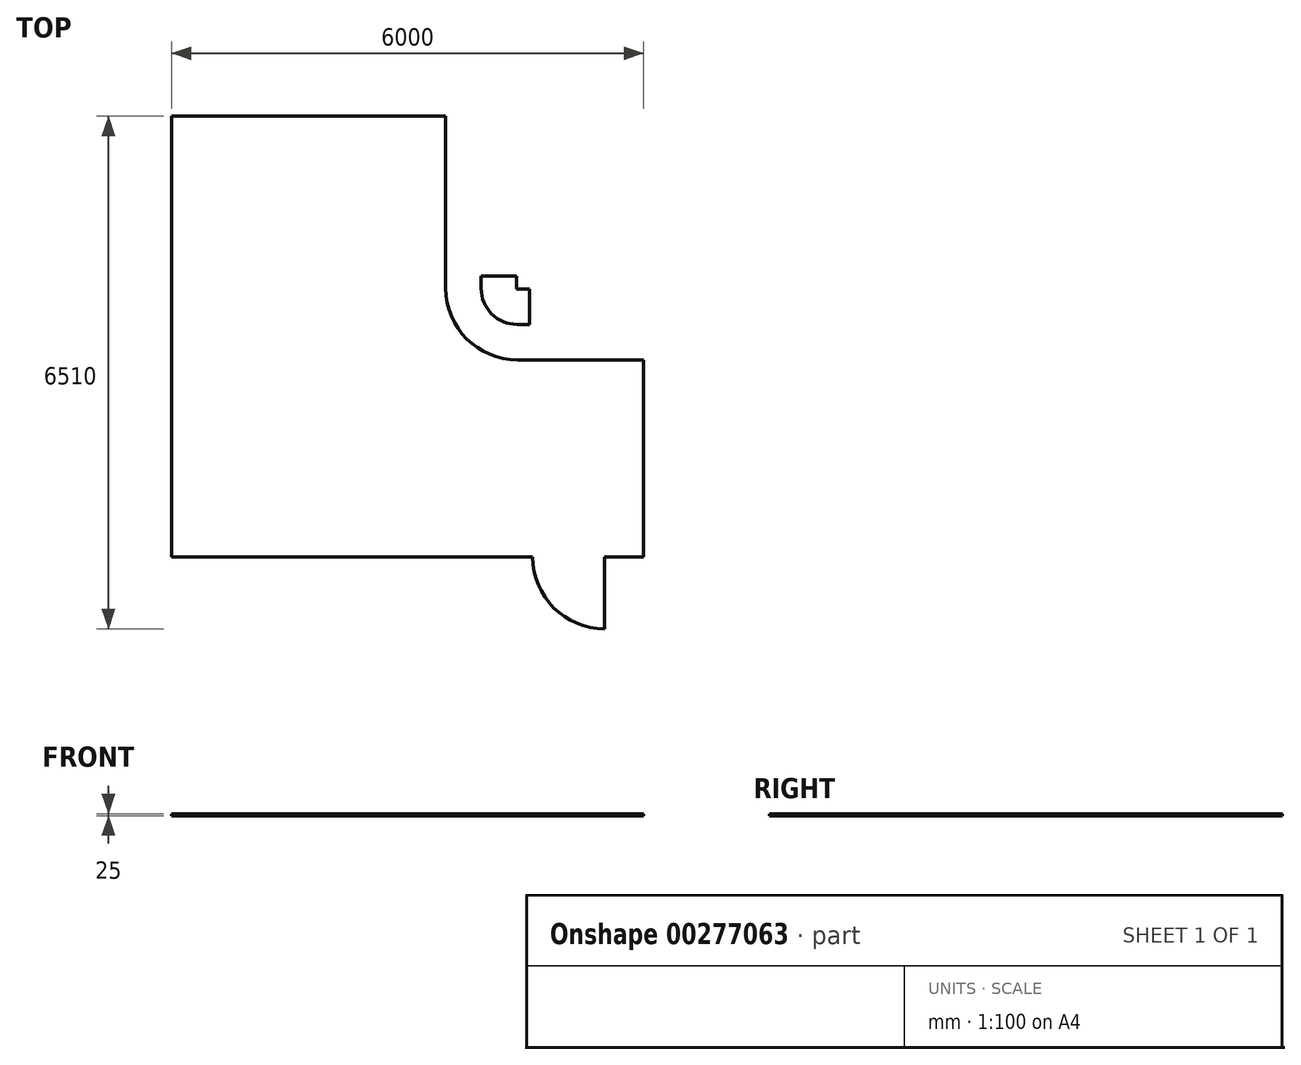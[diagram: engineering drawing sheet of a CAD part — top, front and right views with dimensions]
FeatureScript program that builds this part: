
annotation { "Feature Type Name" : "Feature", "Feature Type Description" : "" }
export const myFeature = defineFeature(function(context is Context, id is Id, definition is map)
    precondition{}
    {
        {
            var Q0;
            Q0=qCreatedBy(makeId("Top.planeOp"),FACE);
            var sketch = newSketch(context, id + "F0", { "sketchPlane" : qUnion([Q0])});
            skLineSegment(sketch, "E0", {"start": v(0, 0) * mm, "end": v(4590, 0) * mm});
            skLineSegment(sketch, "E1", {"start": v(6000, 0) * mm, "end": v(6000, 2505) * mm});
            skLineSegment(sketch, "E2", {"start": v(0, 0) * mm, "end": v(0, 5600) * mm});
            skLineSegment(sketch, "E3", {"start": v(0, 5600) * mm, "end": v(3485, 5600) * mm});
            skLineSegment(sketch, "E4", {"start": v(6000, 2505) * mm, "end": v(6000, 3405) * mm});
            skLineSegment(sketch, "E5", {"start": v(6000, 2505) * mm, "end": v(4395, 2505) * mm});
            skLineSegment(sketch, "E6", {"start": v(3485, 5600) * mm, "end": v(3485, 5527.98) * mm});
            skPoint(sketch, "E7.end.orphan", {"position": v(3485, 5527.98) * mm});
            skLineSegment(sketch, "E8", {"start": v(3485, 3415) * mm, "end": v(3485, 5600) * mm});
            skLineSegment(sketch, "E9", {"start": v(3485, 5600) * mm, "end": v(4385, 5600) * mm});
            skLineSegment(sketch, "E10", {"start": v(4385, 5600) * mm, "end": v(4385, 3405) * mm});
            skLineSegment(sketch, "E11", {"start": v(6000, 3405) * mm, "end": v(4385, 3405) * mm});
            skLineSegment(sketch, "E12", {"start": v(6000, 3405) * mm, "end": v(6000, 2955) * mm});
            skLineSegment(sketch, "E13", {"start": v(6000, 2955) * mm, "end": v(4385, 2955) * mm});
            skLineSegment(sketch, "E14", {"start": v(3935, 5600) * mm, "end": v(3935, 3410) * mm});
            skLineSegment(sketch, "E15", {"start": v(3485, 5600) * mm, "end": v(3485, 5310) * mm});
            skLineSegment(sketch, "E16", {"start": v(3485, 5310) * mm, "end": v(4385, 5310) * mm});
            skLineSegment(sketch, "E17", {"start": v(4385, 5310) * mm, "end": v(4385, 5020) * mm});
            skLineSegment(sketch, "E18", {"start": v(4385, 5020) * mm, "end": v(3485, 5020) * mm});
            skLineSegment(sketch, "E19", {"start": v(3485, 5020) * mm, "end": v(3485, 4730) * mm});
            skLineSegment(sketch, "E20", {"start": v(3485, 4730) * mm, "end": v(4385, 4730) * mm});
            skLineSegment(sketch, "E21", {"start": v(4385, 4730) * mm, "end": v(4385, 4440) * mm});
            skLineSegment(sketch, "E22", {"start": v(4385, 4440) * mm, "end": v(3485, 4440) * mm});
            skLineSegment(sketch, "E23", {"start": v(3485, 4440) * mm, "end": v(3485, 4150) * mm});
            skLineSegment(sketch, "E24", {"start": v(3485, 4150) * mm, "end": v(4385, 4150) * mm});
            skLineSegment(sketch, "E25", {"start": v(4385, 4150) * mm, "end": v(4385, 3860) * mm});
            skLineSegment(sketch, "E26", {"start": v(4385, 3860) * mm, "end": v(3485, 3860) * mm});
            skLineSegment(sketch, "E27", {"start": v(3485, 3860) * mm, "end": v(3485, 3570) * mm});
            skLineSegment(sketch, "E28", {"start": v(3485, 3570) * mm, "end": v(4385, 3570) * mm});
            skLineSegment(sketch, "E29", {"start": v(4390, 2955) * mm, "end": v(4385, 2955) * mm});
            skArc(sketch, "E30.filletArc", {"start": v(3935, 3410) * mm, "mid": v(4068.27, 3088.27) * mm, "end": v(4390, 2955) * mm});
            skPoint(sketch, "E31.visualSharp", {"position": v(3485, 2505) * mm});
            skArc(sketch, "E31.filletArc", {"start": v(3485, 3415) * mm, "mid": v(3751.53, 2771.53) * mm, "end": v(4395, 2505) * mm});
            skLineSegment(sketch, "E32", {"start": v(6000, 3405) * mm, "end": v(5710, 3405) * mm});
            skLineSegment(sketch, "E33", {"start": v(5710, 3405) * mm, "end": v(5710, 2505) * mm});
            skLineSegment(sketch, "E34", {"start": v(5710, 2505) * mm, "end": v(5420, 2505) * mm});
            skLineSegment(sketch, "E35", {"start": v(5420, 2505) * mm, "end": v(5420, 3405) * mm});
            skLineSegment(sketch, "E36", {"start": v(5420, 3405) * mm, "end": v(5130, 3405) * mm});
            skLineSegment(sketch, "E37", {"start": v(5130, 3405) * mm, "end": v(5130, 2505) * mm});
            skLineSegment(sketch, "E38", {"start": v(5130, 2505) * mm, "end": v(4840, 2505) * mm});
            skLineSegment(sketch, "E39", {"start": v(4840, 2505) * mm, "end": v(4840, 3405) * mm});
            skLineSegment(sketch, "E40", {"start": v(4840, 3405) * mm, "end": v(4550, 3405) * mm});
            skLineSegment(sketch, "E41", {"start": v(4550, 3405) * mm, "end": v(4550, 2505) * mm});
            skLineSegment(sketch, "E42.trimOffspring", {"start": v(4385, 2505.05) * mm, "end": v(4385, 2505) * mm});
            skLineSegment(sketch, "E43.trimOffspring", {"start": v(4385, 2955.03) * mm, "end": v(4385, 2955) * mm});
            skLineSegment(sketch, "E44", {"start": v(4385, 5600) * mm, "end": v(4435, 5600) * mm});
            skLineSegment(sketch, "E45", {"start": v(4435, 5600) * mm, "end": v(4435, 3455) * mm});
            skLineSegment(sketch, "E46", {"start": v(6000, 3405) * mm, "end": v(6000, 3455) * mm});
            skLineSegment(sketch, "E47", {"start": v(6000, 3455) * mm, "end": v(4435, 3455) * mm});
            skPoint(sketch, "E48.orphan", {"position": v(4385, 3455) * mm});
            skLineSegment(sketch, "E49", {"start": v(6000, 0) * mm, "end": v(5500, 0) * mm});
            skLineSegment(sketch, "E50", {"start": v(5500, 0) * mm, "end": v(5500, -910) * mm});
            skArc(sketch, "E51", {"start": v(4590, 0) * mm, "mid": v(4856.53, -643.47) * mm, "end": v(5500, -910) * mm});
            skLineSegment(sketch, "E52.trimOffspring", {"start": v(5500, 0) * mm, "end": v(6000, 0) * mm});
            skSolve(sketch);
        }
        {
            var Q0;
            {var subQ5=sQuery(id+"F0.wireOp",EDGE,"E10");var subQ7=sQuery(id+"F0.wireOp",EDGE,"E11");var subQ8=makeQuery(id+"F0.imprint","INTERSECT",VERTEX,{"derivedFrom":[subQ5,subQ7]});Q0=makeQuery(id+"F0.imprint","IMPRINT",FACE,{"disambiguationData":[TD([[makeQuery(id+"F0.imprint","IMPRINT",EDGE,{"disambiguationData":[TD([[subQ8,1.0]])],"derivedFrom":subQ5}),-1.0]])]});}
            var Q1;
            {var subQ9=sQuery(id+"F0.wireOp",EDGE,"E29");Q1=makeQuery(id+"F0.imprint","IMPRINT",FACE,{"disambiguationData":[TD([[makeQuery(id+"F0.imprint","IMPRINT",EDGE,{"derivedFrom":subQ9}),1.0]])]});}
            var Q2;
            Q2=makeQuery(id+"F0.imprint","IMPRINT",FACE,{"disambiguationData":[TD([[makeQuery(id+"F0.imprint","IMPRINT",EDGE,{"derivedFrom":sQuery(id+"F0.wireOp",EDGE,"E0")}),1.0]])]});
            extrude(context, id + "F1", {"entities" : qUnion([Q0, Q1, Q2]), "depth" : 25 * mm});
        }
    });
